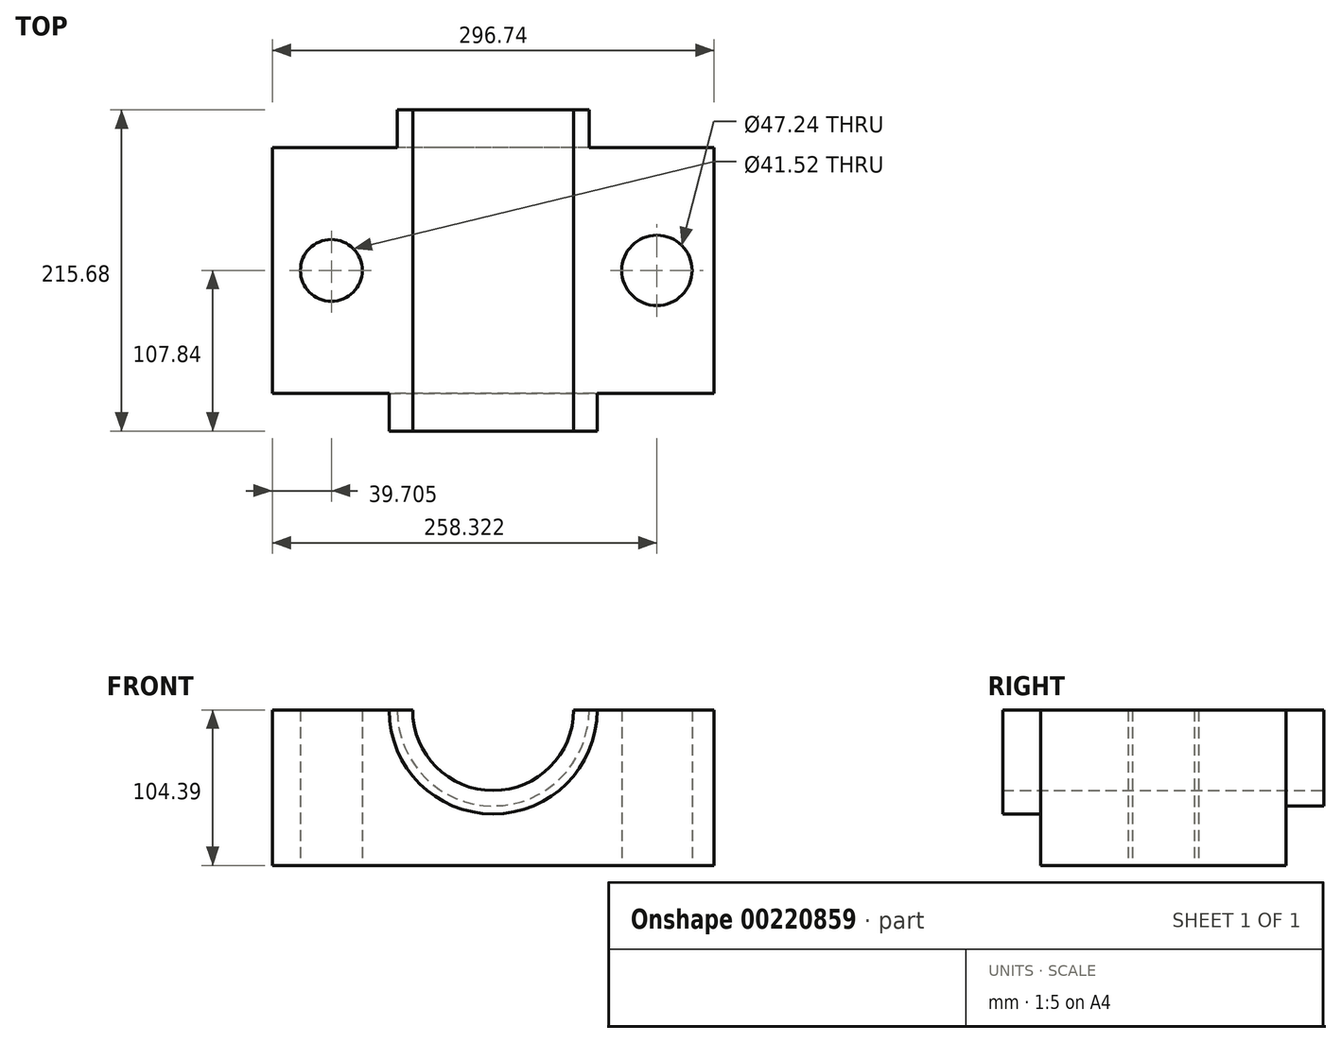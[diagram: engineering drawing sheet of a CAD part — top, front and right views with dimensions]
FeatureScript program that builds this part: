
annotation { "Feature Type Name" : "Feature", "Feature Type Description" : "" }
export const myFeature = defineFeature(function(context is Context, id is Id, definition is map)
    precondition{}
    {
        {
            var Q0;
            Q0=qCreatedBy(makeId("Top.planeOp"),FACE);
            var sketch = newSketch(context, id + "F0", { "sketchPlane" : qUnion([Q0])});
            skLineSegment(sketch, "E0.bottom", {"start": v(148.37, -82.44) * mm, "end": v(-148.37, -82.44) * mm});
            skLineSegment(sketch, "E0.top", {"start": v(148.37, 82.44) * mm, "end": v(-148.37, 82.44) * mm});
            skLineSegment(sketch, "E0.left", {"start": v(148.37, -82.44) * mm, "end": v(148.37, 82.44) * mm});
            skLineSegment(sketch, "E0.right", {"start": v(-148.37, -82.44) * mm, "end": v(-148.37, 82.44) * mm});
            skPoint(sketch, "E0.middle", {"position": v(0, 0) * mm});
            skCircle(sketch, "E1", {"center": v(109.95, 0) * mm, "radius": 23.62 * mm});
            skCircle(sketch, "E2", {"center": v(-108.67, 0) * mm, "radius": 20.76 * mm});
            skSolve(sketch);
        }
        {
            var Q0;
            Q0 = qSketchRegion(id + "F0", true);
            extrude(context, id + "F1", {"entities" : qUnion([Q0]), "depth" : 104.4 * mm});
        }
        {
            var Q0;
            Q0=makeQuery(id+"F1.opExtrude","SWEPT_FACE",FACE,{"disambiguationData":[OSD([sQuery(id+"F0.wireOp",EDGE,"E0.bottom")])]});
            var sketch = newSketch(context, id + "F2", { "sketchPlane" : qUnion([Q0])});
            skCircle(sketch, "E3", {"center": v(0, 104.4) * mm, "radius": 69.83 * mm});
            skCircle(sketch, "E4", {"center": v(0, 104.4) * mm, "radius": 54.08 * mm});
            skSolve(sketch);
        }
        {
            var Q0;
            {var subQ0=sQuery(id+"F2.wireOp",EDGE,"E3");var subQ1=makeQuery(id+"F1.opExtrude","CAP_EDGE",EDGE,{"disambiguationData":[OSD([sQuery(id+"F0.wireOp",EDGE,"E0.bottom")])],"isStart":false});var subQ2=makeQuery(id+"F2.imprint","INTERSECT",VERTEX,{"disambiguationData":[OD(0.0)],"derivedFrom":[subQ1,subQ0]});Q0=makeQuery(id+"F2.imprint","IMPRINT",FACE,{"disambiguationData":[TD([[makeQuery(id+"F2.imprint","IMPRINT",EDGE,{"disambiguationData":[TD([[subQ2,1.0]])],"derivedFrom":subQ0}),1.0]])]});}
            extrude(context, id + "F3", {"entities" : qUnion([Q0]), "operationType" : NewBodyOperationType.ADD, "depth" : 25.4 * mm});
        }
        {
            var Q0;
            Q0=makeQuery(id+"F1.opExtrude","SWEPT_FACE",FACE,{"disambiguationData":[OSD([sQuery(id+"F0.wireOp",EDGE,"E0.top")])]});
            var sketch = newSketch(context, id + "F4", { "sketchPlane" : qUnion([Q0])});
            skCircle(sketch, "E5", {"center": v(0, 104.4) * mm, "radius": 53.35 * mm});
            skCircle(sketch, "E6", {"center": v(0, 104.4) * mm, "radius": 64.38 * mm});
            skSolve(sketch);
        }
        {
            var Q0;
            {var subQ0=sQuery(id+"F4.wireOp",EDGE,"E5");var subQ1=makeQuery(id+"F1.opExtrude","CAP_EDGE",EDGE,{"disambiguationData":[OSD([sQuery(id+"F0.wireOp",EDGE,"E0.top")])],"isStart":false});var subQ2=makeQuery(id+"F4.imprint","INTERSECT",VERTEX,{"disambiguationData":[OD(0.0)],"derivedFrom":[subQ1,subQ0]});Q0=makeQuery(id+"F4.imprint","IMPRINT",FACE,{"disambiguationData":[TD([[makeQuery(id+"F4.imprint","IMPRINT",EDGE,{"disambiguationData":[TD([[subQ2,-1.0]])],"derivedFrom":subQ0}),-1.0]])]});}
            extrude(context, id + "F5", {"entities" : qUnion([Q0]), "operationType" : NewBodyOperationType.ADD, "depth" : 25.4 * mm});
        }
        {
            var Q0;
            {var subQ0=sQuery(id+"F0.wireOp",EDGE,"E0.bottom");var subQ1=sQuery(id+"F2.wireOp",EDGE,"E4");Q0=makeQuery(id+"F3.boolean.opBoolean","SPLIT",FACE,{"disambiguationData":[TD([makeQuery(id+"F3.opExtrude","SWEPT_FACE",FACE,{"disambiguationData":[OSD([subQ1])]})])],"derivedFrom":makeQuery(id+"F1.opExtrude","SWEPT_FACE",FACE,{"disambiguationData":[OSD([subQ0])]})});}
            extrude(context, id + "F6", {"entities" : qUnion([Q0]), "operationType" : NewBodyOperationType.REMOVE, "oppositeDirection" : true, "depth" : 238 * mm});
        }
    });
